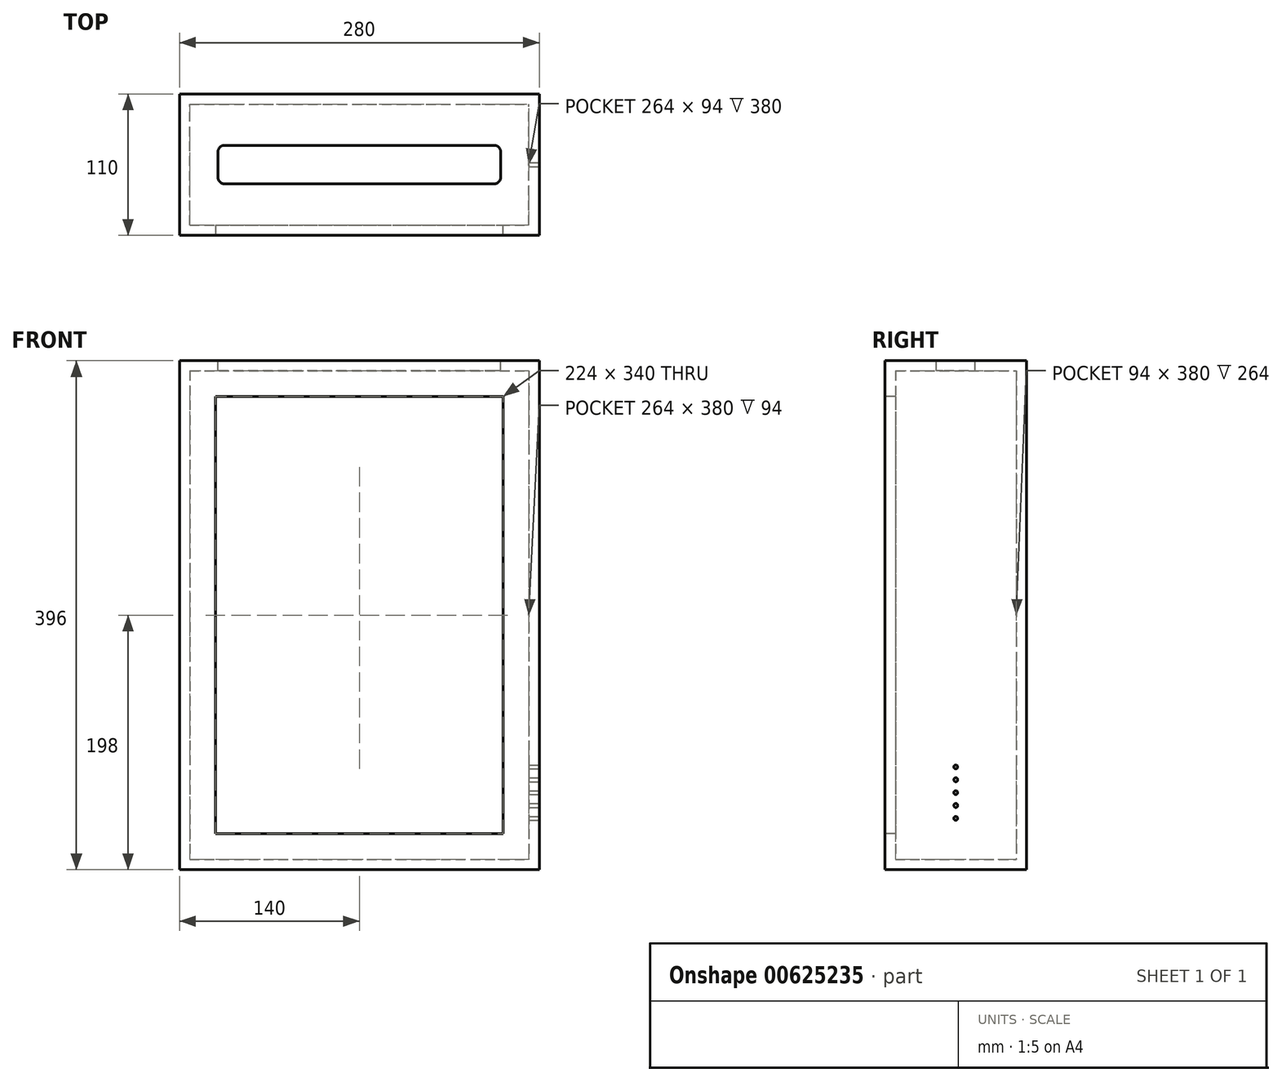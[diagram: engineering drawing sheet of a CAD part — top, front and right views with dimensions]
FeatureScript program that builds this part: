
annotation { "Feature Type Name" : "Feature", "Feature Type Description" : "" }
export const myFeature = defineFeature(function(context is Context, id is Id, definition is map)
    precondition{}
    {
        {
            var Q0;
            Q0=qCreatedBy(makeId("Top.planeOp"),FACE);
            var sketch = newSketch(context, id + "F0", { "sketchPlane" : qUnion([Q0])});
            skLineSegment(sketch, "E0.bottom", {"start": v(-140, 55) * mm, "end": v(140, 55) * mm});
            skLineSegment(sketch, "E0.top", {"start": v(-140, -55) * mm, "end": v(140, -55) * mm});
            skLineSegment(sketch, "E0.left", {"start": v(-140, 55) * mm, "end": v(-140, -55) * mm});
            skLineSegment(sketch, "E0.right", {"start": v(140, 55) * mm, "end": v(140, -55) * mm});
            skPoint(sketch, "E0.middle", {"position": v(0, 0) * mm});
            skSolve(sketch);
        }
        {
            var Q0;
            Q0=makeQuery(id+"F0.imprint","IMPRINT",FACE,{"disambiguationData":[TD([[makeQuery(id+"F0.imprint","IMPRINT",EDGE,{"derivedFrom":sQuery(id+"F0.wireOp",EDGE,"E0.bottom")}),-1.0]])]});
            var Q1;
            Q1 = qSketchRegion(id + "F2", true);
            extrude(context, id + "F1", {"entities" : qUnion([Q0, Q1]), "depth" : 8 * mm, "offsetDistance" : 25 * mm});
        }
        {
            var Q0;
            Q0=makeQuery(id+"F1.opExtrude","CAP_FACE",FACE,{"disambiguationData":[OSD([sQuery(id+"F0.wireOp",EDGE,"E0.bottom"),sQuery(id+"F0.wireOp",EDGE,"E0.top"),sQuery(id+"F0.wireOp",EDGE,"E0.left"),sQuery(id+"F0.wireOp",EDGE,"E0.right")])],"isStart":false});
            var sketch = newSketch(context, id + "F2", { "sketchPlane" : qUnion([Q0])});
            skLineSegment(sketch, "E1.bottom", {"start": v(-140, -55) * mm, "end": v(140, -55) * mm});
            skLineSegment(sketch, "E1.top", {"start": v(-140, 55) * mm, "end": v(140, 55) * mm});
            skLineSegment(sketch, "E1.left", {"start": v(-140, -55) * mm, "end": v(-140, 55) * mm});
            skLineSegment(sketch, "E1.right", {"start": v(140, -55) * mm, "end": v(140, 55) * mm});
            skPoint(sketch, "E1.middle", {"position": v(0, 0) * mm});
            skLineSegment(sketch, "E2.bottom", {"start": v(-132, -47) * mm, "end": v(132, -47) * mm});
            skLineSegment(sketch, "E2.top", {"start": v(-132, 47) * mm, "end": v(132, 47) * mm});
            skLineSegment(sketch, "E2.left", {"start": v(-132, -47) * mm, "end": v(-132, 47) * mm});
            skLineSegment(sketch, "E2.right", {"start": v(132, -47) * mm, "end": v(132, 47) * mm});
            skSolve(sketch);
        }
        {
            var Q0;
            Q0=makeQuery(id+"F2.imprint","IMPRINT",FACE,{"disambiguationData":[TD([[makeQuery(id+"F2.imprint","IMPRINT",EDGE,{"derivedFrom":sQuery(id+"F2.wireOp",EDGE,"E1.bottom")}),1.0]])]});
            extrude(context, id + "F3", {"entities" : qUnion([Q0]), "operationType" : NewBodyOperationType.ADD, "depth" : 20 * mm});
        }
        {
            var Q0;
            Q0=makeQuery(id+"F3.opExtrude","CAP_FACE",FACE,{"disambiguationData":[OSD([sQuery(id+"F2.wireOp",EDGE,"E1.bottom"),sQuery(id+"F2.wireOp",EDGE,"E1.top"),sQuery(id+"F2.wireOp",EDGE,"E1.left"),sQuery(id+"F2.wireOp",EDGE,"E1.right"),sQuery(id+"F2.wireOp",EDGE,"E2.bottom"),sQuery(id+"F2.wireOp",EDGE,"E2.top"),sQuery(id+"F2.wireOp",EDGE,"E2.left"),sQuery(id+"F2.wireOp",EDGE,"E2.right")])],"isStart":false});
            var sketch = newSketch(context, id + "F4", { "sketchPlane" : qUnion([Q0])});
            skLineSegment(sketch, "E3", {"start": v(-132, 47) * mm, "end": v(-132, -47) * mm});
            skLineSegment(sketch, "E4", {"start": v(-132, -47) * mm, "end": v(-112, -47) * mm});
            skLineSegment(sketch, "E5", {"start": v(-112, -47) * mm, "end": v(-112, -55) * mm});
            skLineSegment(sketch, "E6", {"start": v(-112, -55) * mm, "end": v(-140, -55) * mm});
            skLineSegment(sketch, "E7", {"start": v(-140, -55) * mm, "end": v(-140, 55) * mm});
            skLineSegment(sketch, "E8", {"start": v(-140, 55) * mm, "end": v(140, 55) * mm});
            skLineSegment(sketch, "E9", {"start": v(140, 55) * mm, "end": v(140, -55) * mm});
            skLineSegment(sketch, "E10", {"start": v(140, -55) * mm, "end": v(112, -55) * mm});
            skLineSegment(sketch, "E11", {"start": v(112, -55) * mm, "end": v(112, -47) * mm});
            skLineSegment(sketch, "E12", {"start": v(112, -47) * mm, "end": v(132, -47) * mm});
            skLineSegment(sketch, "E13", {"start": v(132, -47) * mm, "end": v(132, 47) * mm});
            skLineSegment(sketch, "E14", {"start": v(132, 47) * mm, "end": v(-132, 47) * mm});
            skSolve(sketch);
        }
        {
            var Q0;
            Q0=makeQuery(id+"F4.imprint","IMPRINT",FACE,{"disambiguationData":[TD([[makeQuery(id+"F4.imprint","IMPRINT",EDGE,{"derivedFrom":sQuery(id+"F4.wireOp",EDGE,"E3")}),1.0]])]});
            extrude(context, id + "F5", {"entities" : qUnion([Q0]), "operationType" : NewBodyOperationType.ADD, "depth" : 340 * mm});
        }
        {
            var Q0;
            Q0=makeQuery(id+"F5.opExtrude","CAP_FACE",FACE,{"disambiguationData":[OSD([sQuery(id+"F4.wireOp",EDGE,"E3"),sQuery(id+"F4.wireOp",EDGE,"E4"),sQuery(id+"F4.wireOp",EDGE,"E5"),sQuery(id+"F4.wireOp",EDGE,"E6"),sQuery(id+"F4.wireOp",EDGE,"E7"),sQuery(id+"F4.wireOp",EDGE,"E8"),sQuery(id+"F4.wireOp",EDGE,"E9"),sQuery(id+"F4.wireOp",EDGE,"E10"),sQuery(id+"F4.wireOp",EDGE,"E11"),sQuery(id+"F4.wireOp",EDGE,"E12"),sQuery(id+"F4.wireOp",EDGE,"E13"),sQuery(id+"F4.wireOp",EDGE,"E14")])],"isStart":false});
            var sketch = newSketch(context, id + "F6", { "sketchPlane" : qUnion([Q0])});
            skLineSegment(sketch, "E15.bottom", {"start": v(-132, -47) * mm, "end": v(132, -47) * mm});
            skLineSegment(sketch, "E15.top", {"start": v(-132, 47) * mm, "end": v(132, 47) * mm});
            skLineSegment(sketch, "E15.left", {"start": v(-132, -47) * mm, "end": v(-132, 47) * mm});
            skLineSegment(sketch, "E15.right", {"start": v(132, -47) * mm, "end": v(132, 47) * mm});
            skPoint(sketch, "E15.middle", {"position": v(0, 0) * mm});
            skLineSegment(sketch, "E16.bottom", {"start": v(-140, -55) * mm, "end": v(140, -55) * mm});
            skLineSegment(sketch, "E16.top", {"start": v(-140, 55) * mm, "end": v(140, 55) * mm});
            skLineSegment(sketch, "E16.left", {"start": v(-140, -55) * mm, "end": v(-140, 55) * mm});
            skLineSegment(sketch, "E16.right", {"start": v(140, -55) * mm, "end": v(140, 55) * mm});
            skSolve(sketch);
        }
        {
            var Q0;
            {var subQ1=makeQuery(id+"F5.opExtrude","CAP_EDGE",EDGE,{"disambiguationData":[OSD([sQuery(id+"F4.wireOp",EDGE,"E5")])],"isStart":false});Q0=makeQuery(id+"F6.imprint","IMPRINT",FACE,{"disambiguationData":[TD([[makeQuery(id+"F6.imprint","IMPRINT",EDGE,{"derivedFrom":subQ1}),1.0]])]});}
            var Q1;
            Q1=makeQuery(id+"F6.imprint","IMPRINT",FACE,{"disambiguationData":[TD([[makeQuery(id+"F6.imprint","IMPRINT",EDGE,{"derivedFrom":sQuery(id+"F6.wireOp",EDGE,"E15.top")}),1.0]])]});
            var Q2;
            Q2=qSketchRegion(id+"F8",true);
            extrude(context, id + "F7", {"entities" : qUnion([Q0, Q1, Q2]), "operationType" : NewBodyOperationType.ADD, "depth" : 20 * mm, "offsetDistance" : 25 * mm});
        }
        {
            var Q0;
            Q0=makeQuery(id+"F7.opExtrude","CAP_FACE",FACE,{"disambiguationData":[OSD([sQuery(id+"F6.wireOp",EDGE,"E15.bottom"),sQuery(id+"F6.wireOp",EDGE,"E15.top"),sQuery(id+"F6.wireOp",EDGE,"E15.left"),sQuery(id+"F6.wireOp",EDGE,"E15.right"),sQuery(id+"F6.wireOp",EDGE,"E16.bottom"),sQuery(id+"F6.wireOp",EDGE,"E16.top"),sQuery(id+"F6.wireOp",EDGE,"E16.left"),sQuery(id+"F6.wireOp",EDGE,"E16.right")])],"isStart":false});
            var sketch = newSketch(context, id + "F8", { "sketchPlane" : qUnion([Q0])});
            skLineSegment(sketch, "E17.bottom", {"start": v(-140, -55) * mm, "end": v(140, -55) * mm});
            skLineSegment(sketch, "E17.top", {"start": v(-140, 55) * mm, "end": v(140, 55) * mm});
            skLineSegment(sketch, "E17.left", {"start": v(-140, -55) * mm, "end": v(-140, 55) * mm});
            skLineSegment(sketch, "E17.right", {"start": v(140, -55) * mm, "end": v(140, 55) * mm});
            skPoint(sketch, "E17.middle", {"position": v(0, 0) * mm});
            skSolve(sketch);
        }
        {
            var Q0;
            Q0=makeQuery(id+"F8.imprint","IMPRINT",FACE,{"disambiguationData":[TD([[makeQuery(id+"F8.imprint","IMPRINT",EDGE,{"derivedFrom":sQuery(id+"F8.wireOp",EDGE,"E17.bottom")}),1.0]])]});
            var Q1;
            Q1=makeQuery(id+"F8.imprint","IMPRINT",FACE,{"disambiguationData":[TD([[makeQuery(id+"F8.imprint","IMPRINT",EDGE,{"derivedFrom":makeQuery(id+"F7.opExtrude","CAP_EDGE",EDGE,{"disambiguationData":[OSD([sQuery(id+"F6.wireOp",EDGE,"E15.bottom")])],"isStart":false})}),1.0]])]});
            extrude(context, id + "F9", {"entities" : qUnion([Q0, Q1]), "operationType" : NewBodyOperationType.ADD, "depth" : 8 * mm, "offsetDistance" : 25 * mm});
        }
        {
            var Q0;
            Q0=makeQuery(id+"F9.boolean.opBoolean","MERGE",FACE,{"derivedFrom":[makeQuery(id+"F7.boolean.opBoolean","MERGE",FACE,{"derivedFrom":[makeQuery(id+"F5.boolean.opBoolean","MERGE",FACE,{"derivedFrom":[makeQuery(id+"F3.boolean.opBoolean","MERGE",FACE,{"derivedFrom":[makeQuery(id+"F1.opExtrude","SWEPT_FACE",FACE,{"disambiguationData":[OSD([sQuery(id+"F0.wireOp",EDGE,"E0.right")])]}),makeQuery(id+"F3.opExtrude","SWEPT_FACE",FACE,{"disambiguationData":[OSD([sQuery(id+"F2.wireOp",EDGE,"E1.right")])]})]}),makeQuery(id+"F5.opExtrude","SWEPT_FACE",FACE,{"disambiguationData":[OSD([sQuery(id+"F4.wireOp",EDGE,"E9")])]})]}),makeQuery(id+"F7.opExtrude","SWEPT_FACE",FACE,{"disambiguationData":[OSD([sQuery(id+"F6.wireOp",EDGE,"E16.right")])]})]}),makeQuery(id+"F9.opExtrude","SWEPT_FACE",FACE,{"disambiguationData":[OSD([sQuery(id+"F8.wireOp",EDGE,"E17.right")])]})]});
            var sketch = newSketch(context, id + "F10", { "sketchPlane" : qUnion([Q0])});
            skLineSegment(sketch, "E18", {"start": v(0, 0) * mm, "end": v(0, 396) * mm, "construction": true});
            skCircle(sketch, "E19", {"center": v(0, 40) * mm, "radius": 1.55 * mm});
            skCircle(sketch, "E20", {"center": v(0, 50) * mm, "radius": 1.55 * mm});
            skCircle(sketch, "E21", {"center": v(0, 60) * mm, "radius": 1.55 * mm});
            skCircle(sketch, "E22", {"center": v(0, 70) * mm, "radius": 1.55 * mm});
            skCircle(sketch, "E23", {"center": v(0, 80) * mm, "radius": 1.55 * mm});
            skSolve(sketch);
        }
        {
            var Q0;
            Q0=makeQuery(id+"F10.imprint","IMPRINT",FACE,{"disambiguationData":[TD([[makeQuery(id+"F10.imprint","IMPRINT",EDGE,{"derivedFrom":sQuery(id+"F10.wireOp",EDGE,"E23")}),1.0]])]});
            var Q1;
            Q1=makeQuery(id+"F10.imprint","IMPRINT",FACE,{"disambiguationData":[TD([[makeQuery(id+"F10.imprint","IMPRINT",EDGE,{"derivedFrom":sQuery(id+"F10.wireOp",EDGE,"E22")}),1.0]])]});
            var Q2;
            Q2=makeQuery(id+"F10.imprint","IMPRINT",FACE,{"disambiguationData":[TD([[makeQuery(id+"F10.imprint","IMPRINT",EDGE,{"derivedFrom":sQuery(id+"F10.wireOp",EDGE,"E20")}),1.0]])]});
            var Q3;
            Q3=makeQuery(id+"F10.imprint","IMPRINT",FACE,{"disambiguationData":[TD([[makeQuery(id+"F10.imprint","IMPRINT",EDGE,{"derivedFrom":sQuery(id+"F10.wireOp",EDGE,"E19")}),1.0]])]});
            var Q4;
            Q4=makeQuery(id+"F10.imprint","IMPRINT",FACE,{"disambiguationData":[TD([[makeQuery(id+"F10.imprint","IMPRINT",EDGE,{"derivedFrom":sQuery(id+"F10.wireOp",EDGE,"E21")}),1.0]])]});
            extrude(context, id + "F11", {"entities" : qUnion([Q0, Q1, Q2, Q3, Q4]), "operationType" : NewBodyOperationType.REMOVE, "endBound" : BoundingType.UP_TO_NEXT, "oppositeDirection" : true, "depth" : 25 * mm, "offsetDistance" : 25 * mm});
        }
        {
            var Q0;
            Q0=makeQuery(id+"F9.opExtrude","CAP_FACE",FACE,{"disambiguationData":[OSD([sQuery(id+"F8.wireOp",EDGE,"E17.bottom"),sQuery(id+"F8.wireOp",EDGE,"E17.top"),sQuery(id+"F8.wireOp",EDGE,"E17.left"),sQuery(id+"F8.wireOp",EDGE,"E17.right")])],"isStart":false});
            var sketch = newSketch(context, id + "F12", { "sketchPlane" : qUnion([Q0])});
            skLineSegment(sketch, "E24.bottom", {"start": v(-110, -15) * mm, "end": v(110, -15) * mm});
            skLineSegment(sketch, "E24.top", {"start": v(-110, 15) * mm, "end": v(110, 15) * mm});
            skLineSegment(sketch, "E24.left", {"start": v(-110, -15) * mm, "end": v(-110, 15) * mm});
            skLineSegment(sketch, "E24.right", {"start": v(110, -15) * mm, "end": v(110, 15) * mm});
            skPoint(sketch, "E24.middle", {"position": v(0, 0) * mm});
            skSolve(sketch);
        }
        {
            var Q0;
            Q0=makeQuery(id+"F12.imprint","IMPRINT",FACE,{"disambiguationData":[TD([[makeQuery(id+"F12.imprint","IMPRINT",EDGE,{"derivedFrom":sQuery(id+"F12.wireOp",EDGE,"E24.bottom")}),1.0]])]});
            extrude(context, id + "F13", {"entities" : qUnion([Q0]), "operationType" : NewBodyOperationType.REMOVE, "endBound" : BoundingType.UP_TO_NEXT, "oppositeDirection" : true, "depth" : 25 * mm, "offsetDistance" : 25 * mm});
        }
        {
            var Q0;
            Q0=makeQuery(id+"F13.boolean.opBoolean","COPY",EDGE,{"derivedFrom":makeQuery(id+"F13.opExtrude","SWEPT_EDGE",EDGE,{"disambiguationData":[OSD([sQuery(id+"F12.wireOp",EDGE,"E24.top"),sQuery(id+"F12.wireOp",EDGE,"E24.left")])]})});
            var Q1;
            Q1=makeQuery(id+"F13.boolean.opBoolean","COPY",EDGE,{"derivedFrom":makeQuery(id+"F13.opExtrude","SWEPT_EDGE",EDGE,{"disambiguationData":[OSD([sQuery(id+"F12.wireOp",EDGE,"E24.bottom"),sQuery(id+"F12.wireOp",EDGE,"E24.left")])]})});
            var Q2;
            Q2=makeQuery(id+"F13.boolean.opBoolean","COPY",EDGE,{"derivedFrom":makeQuery(id+"F13.opExtrude","SWEPT_EDGE",EDGE,{"disambiguationData":[OSD([sQuery(id+"F12.wireOp",EDGE,"E24.bottom"),sQuery(id+"F12.wireOp",EDGE,"E24.right")])]})});
            var Q3;
            Q3=makeQuery(id+"F13.boolean.opBoolean","COPY",EDGE,{"derivedFrom":makeQuery(id+"F13.opExtrude","SWEPT_EDGE",EDGE,{"disambiguationData":[OSD([sQuery(id+"F12.wireOp",EDGE,"E24.top"),sQuery(id+"F12.wireOp",EDGE,"E24.right")])]})});
            fillet(context, id + "F14", {"entities" : qUnion([Q0, Q1, Q2, Q3]), "radius" : 5 * mm, "tangentPropagation" : true, "allowEdgeOverflow" : false});
        }
    });
